# Revit family: STORA-LK_D1900
name_source: partatom
category: Leuchten
revit_build: Autodesk Revit 2017 (Build: 20160225_1515(x64)
units: mm (PartAtom-declared; Revit-internal decimal feet)

## family parameters
Basisbauteil = Fläche
Beim Laden mit Abzugskörper schneiden = Nein
Bemaßung runder Anschluss = Durchmesser verwenden
Gemeinsam genutzt = Nein
Lichtquelle = Ja
OmniClass-Nummer = 23.80.70.11
OmniClass-Titel = Luminaries for Internal Lighting
Raumberechnungspunkt = Nein
Teiletyp = Normal

## types (8) — shared parameters
Beschreibung = Suspended lumnaire
Body = RIDI Metal White 9016
Certification = CE
Cover = RIDI Light Emitting Surface
Diameter = 1900 mm  [stored 6.2336 ft]
Emissionsform beim Rendern sichtbar = Nein
Energy Class = A++ - A
Farbfilter = 16777215
Farbtemperaturverschiebung bei Dämpfen der Lampe = <Keine Auswahl>
Height = 100 mm  [stored 0.328084 ft]
Hersteller = Spectral
IP Rating = IP 20
Lampe = 1xLED-M
Neigungswinkel = -90.00°
Suspension = RIDI Metall silver 9006
Voltage = 230 V
Von Kreisdurchmesser aussenden = 1900 mm  [stored 6.2336 ft]
zero-valued in all types: Vorgabe-Ansicht

## per-type parameters (varying)
| type | Datei für fotometrisches Netz | Indirect | Modell | Number of Poles | Scheinlast | Weight |
| STORA-LK-I-LED D1900/830 OS | STORA-LK-I-LED D1900_840 OS.IES | RIDI Light Emitting Surface | SPC0620023 | 2 | 184 VA | 30 kg |
| STORA-LK-I-LED D1900/840 OS | STORA-LK-I-LED D1900_840 OS.IES | RIDI Light Emitting Surface | SPC0620019 | 2 | 184 VA | 30 kg |
| STORA-LK-LED D1900/840 OS | STORA-LK-LED D1900_840 OS.IES | RIDI Metal White 9016 | SPC0620014 | 1 | 127 VA | 22.5 kg |
| STORA-LK-LED D1900/830 OS | STORA-LK-LED D1900_840 OS.IES | RIDI Metal White 9016 | SPC0620021 | 1 | 127 VA | 22.5 kg |
| STORA-LK-I-LED D1900/830 OS-DA | STORA-LK-I-LED D1900_840 OS.IES | RIDI Light Emitting Surface | SPC0630023 | 1 | 184 VA | 30 kg |
| STORA-LK-I-LED D1900/840 OS-DA | STORA-LK-I-LED D1900_840 OS.IES | RIDI Light Emitting Surface | SPC0630019 | 1 | 184 VA | 30 kg |
| STORA-LK-LED D1900/830 OS-DA | STORA-LK-LED D1900_840 OS.IES | RIDI Metal White 9016 | SPC0630021 | 1 | 127 VA | 22.5 kg |
| STORA-LK-LED D1900/840 OS-DA | STORA-LK-LED D1900_840 OS.IES | RIDI Metal White 9016 | SPC0630014 | 1 | 127 VA | 22.5 kg |

note: [stored X ft] marks values corroborated as IEEE doubles in the binary element streams (Revit-internal decimal feet)

## geometry (parser evidence)
native form markers: Sweep x3
no freeform markers — native parametric forms only
